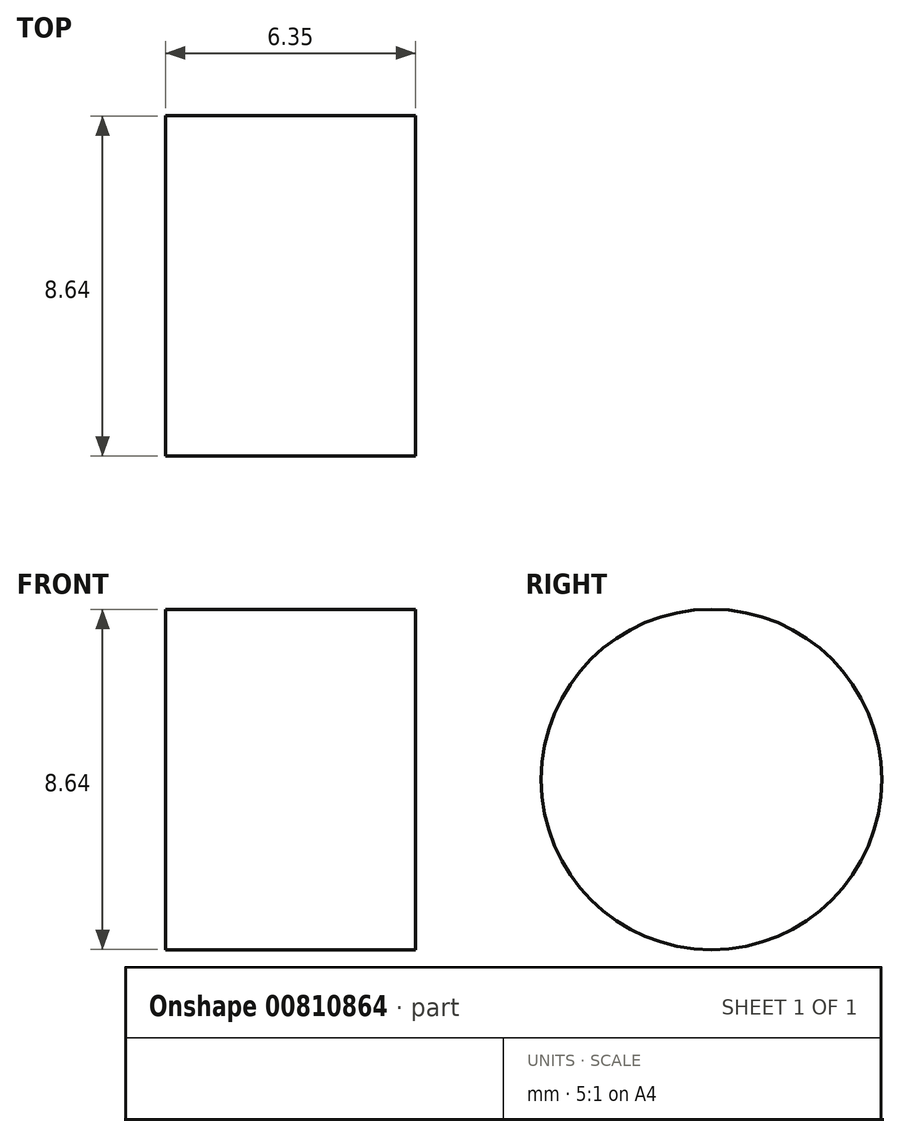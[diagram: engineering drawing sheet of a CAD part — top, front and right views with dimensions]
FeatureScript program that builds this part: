
annotation { "Feature Type Name" : "Feature", "Feature Type Description" : "" }
export const myFeature = defineFeature(function(context is Context, id is Id, definition is map)
    precondition{}
    {
        {
            var Q0;
            Q0=qCreatedBy(makeId("Right.planeOp"),FACE);
            var sketch = newSketch(context, id + "F0", { "sketchPlane" : qUnion([Q0])});
            skCircle(sketch, "E0", {"center": v(0, 0) * mm, "radius": 4.32 * mm});
            skSolve(sketch);
        }
        {
            var Q0;
            Q0=makeQuery(id+"F0.imprint","IMPRINT",FACE,{"disambiguationData":[TD([[makeQuery(id+"F0.imprint","IMPRINT",EDGE,{"derivedFrom":sQuery(id+"F0.wireOp",EDGE,"E0")}),1.0]])]});
            extrude(context, id + "F1", {"entities" : qUnion([Q0]), "depth" : 6.35 * mm, "offsetDistance" : 25.4 * mm});
        }
    });
